# Revit family: en-halla-rotao-suspendedrfa
name_source: partatom
category: Осветительные приборы
revit_build: Autodesk Revit 2017 (Build: 20160225_1515(x64)
units: mm (PartAtom-declared; Revit-internal decimal feet)

## family parameters
Заголовок OmniClass = General Luminaries, Non Directional
Источник света = Нет
Номер OmniClass = 23.80.70.11.11
Общий = Нет
Основа = Грань
При загрузке вырезать с полостями = Нет
Размер круглого соединителя = Использовать диаметр
Тип детали = Нормальный
Точка расчета площади = Нет

## types (1)
- en-halla-rotao-suspendedrfa
    Colour of luminaire = Aluminium - silver
    Date of publishing = 2014-12-14
    Depth = 616.00
    Design country = Czech Republic
    Edition number = 1
    Electric potential = 230 В
    IFC Classification = Light Fixture
    LED source = Да
    Lighting height = 70 мм
    Lighting length = 616 мм
    Lighting width = 616 мм
    Manufacturer country = Czech Republic
    Manufacturer name = HALLA
    Material main = Aluminium
    Material of luminaire = Hliník
    NBS Reference Code = 49
    NBS Reference Description = Luminaires And Lamps
    Nominal height = 70.00
    Nominal width = 616.00
    Number of sources = 1
    Power input = 84 Вт
    Price (EUR) = 0 $
    Product SKU = rotao
    Product family = Indoor Luminaires
    Product group = ROTAO
    QR code = http://file-system.ru
    UNSPSC Code = 3911
    URL = www.halla.cz
    Uniclass 1.4 Code = JY73
    Uniclass 1.4 Description = Luminaires and lamps
    Uniclass 2.0 Code = PR-49
    Uniclass 2.0 Description = Luminaires And Lamps
    Weight Net (Kg) = 0
    Изготовитель = HALLA
    Код по классификатору = D5020200
    Отметка по умолчанию = 0 мм
    Полная установленная мощность = 84 В·А
